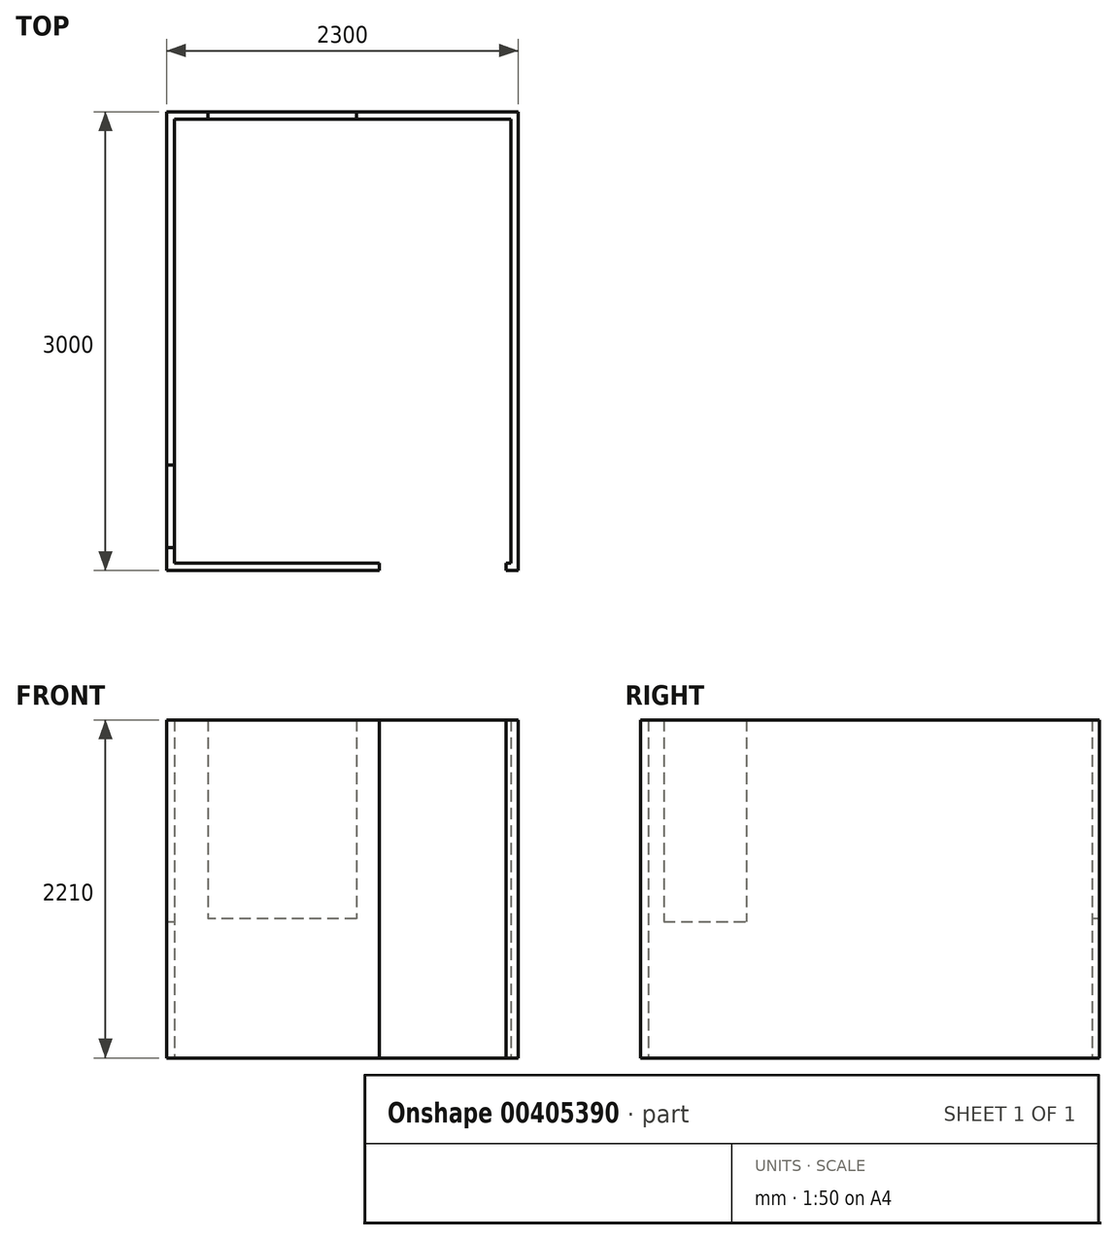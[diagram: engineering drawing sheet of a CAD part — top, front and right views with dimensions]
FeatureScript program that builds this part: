
annotation { "Feature Type Name" : "Feature", "Feature Type Description" : "" }
export const myFeature = defineFeature(function(context is Context, id is Id, definition is map)
    precondition{}
    {
        {
            var Q0;
            Q0=qCreatedBy(makeId("Top.planeOp"),FACE);
            var sketch = newSketch(context, id + "F0", { "sketchPlane" : qUnion([Q0])});
            skLineSegment(sketch, "E0.bottom", {"start": v(1100, -1450) * mm, "end": v(-1100, -1450) * mm});
            skLineSegment(sketch, "E0.top", {"start": v(1100, 1450) * mm, "end": v(-1100, 1450) * mm});
            skLineSegment(sketch, "E0.left", {"start": v(1100, -1450) * mm, "end": v(1100, 1450) * mm});
            skLineSegment(sketch, "E0.right", {"start": v(-1100, -1450) * mm, "end": v(-1100, 1450) * mm});
            skPoint(sketch, "E0.middle", {"position": v(0, 0) * mm});
            skLineSegment(sketch, "E1.0", {"start": v(-1150, -1500) * mm, "end": v(-1150, 1500) * mm});
            skLineSegment(sketch, "E1.1", {"start": v(1150, -1500) * mm, "end": v(-1150, -1500) * mm});
            skLineSegment(sketch, "E1.2", {"start": v(1150, -1500) * mm, "end": v(1150, 1500) * mm});
            skLineSegment(sketch, "E1.3", {"start": v(1150, 1500) * mm, "end": v(-1150, 1500) * mm});
            skLineSegment(sketch, "E2.bottom", {"start": v(1070, -1450) * mm, "end": v(240, -1450) * mm});
            skLineSegment(sketch, "E2.top", {"start": v(1070, -1500) * mm, "end": v(240, -1500) * mm});
            skLineSegment(sketch, "E2.left", {"start": v(1070, -1450) * mm, "end": v(1070, -1500) * mm});
            skLineSegment(sketch, "E2.right", {"start": v(240, -1450) * mm, "end": v(240, -1500) * mm});
            skSolve(sketch);
        }
        {
            var Q0;
            Q0=makeQuery(id+"F0.imprint","IMPRINT",FACE,{"disambiguationData":[TD([[makeQuery(id+"F0.imprint","IMPRINT",EDGE,{"derivedFrom":sQuery(id+"F0.wireOp",EDGE,"E0.top")}),-1.0]])]});
            extrude(context, id + "F1", {"entities" : qUnion([Q0]), "depth" : 890 * mm});
        }
        {
            var Q0;
            Q0=makeQuery(id+"F1.opExtrude","CAP_FACE",FACE,{"disambiguationData":[OSD([sQuery(id+"F0.wireOp",EDGE,"E0.bottom"),sQuery(id+"F0.wireOp",EDGE,"E0.top"),sQuery(id+"F0.wireOp",EDGE,"E0.left"),sQuery(id+"F0.wireOp",EDGE,"E0.right"),sQuery(id+"F0.wireOp",EDGE,"E1.0"),sQuery(id+"F0.wireOp",EDGE,"E1.1"),sQuery(id+"F0.wireOp",EDGE,"E1.2"),sQuery(id+"F0.wireOp",EDGE,"E1.3"),sQuery(id+"F0.wireOp",EDGE,"E2.left"),sQuery(id+"F0.wireOp",EDGE,"E2.right")])],"isStart":false});
            var sketch = newSketch(context, id + "F2", { "sketchPlane" : qUnion([Q0])});
            skLineSegment(sketch, "E3.bottom", {"start": v(-1150, -1350) * mm, "end": v(-1100, -1350) * mm});
            skLineSegment(sketch, "E3.top", {"start": v(-1150, -810) * mm, "end": v(-1100, -810) * mm});
            skLineSegment(sketch, "E3.left", {"start": v(-1150, -1350) * mm, "end": v(-1150, -810) * mm});
            skLineSegment(sketch, "E3.right", {"start": v(-1100, -1350) * mm, "end": v(-1100, -810) * mm});
            skSolve(sketch);
        }
        {
            var Q0;
            {var subQ8=sQuery(id+"F2.wireOp",EDGE,"E3.bottom");Q0=makeQuery(id+"F2.imprint","IMPRINT",FACE,{"disambiguationData":[TD([[makeQuery(id+"F2.imprint","IMPRINT",EDGE,{"derivedFrom":subQ8}),-1.0]])]});}
            var Q1;
            {var subQ5=sQuery(id+"F2.wireOp",EDGE,"E3.top");Q1=makeQuery(id+"F2.imprint","IMPRINT",FACE,{"disambiguationData":[TD([[makeQuery(id+"F2.imprint","IMPRINT",EDGE,{"derivedFrom":subQ5}),1.0]])]});}
            extrude(context, id + "F3", {"entities" : qUnion([Q0, Q1]), "operationType" : NewBodyOperationType.ADD, "depth" : 20 * mm});
        }
        {
            var Q0;
            Q0=makeQuery(id+"F3.opExtrude","CAP_FACE",FACE,{"disambiguationData":[OSD([sQuery(id+"F0.wireOp",EDGE,"E0.bottom"),sQuery(id+"F0.wireOp",EDGE,"E0.top"),sQuery(id+"F0.wireOp",EDGE,"E0.left"),sQuery(id+"F0.wireOp",EDGE,"E0.right"),sQuery(id+"F0.wireOp",EDGE,"E1.0"),sQuery(id+"F0.wireOp",EDGE,"E1.1"),sQuery(id+"F0.wireOp",EDGE,"E1.2"),sQuery(id+"F0.wireOp",EDGE,"E1.3"),sQuery(id+"F0.wireOp",EDGE,"E2.left"),sQuery(id+"F2.wireOp",EDGE,"E3.top")])],"isStart":false});
            var sketch = newSketch(context, id + "F4", { "sketchPlane" : qUnion([Q0])});
            skLineSegment(sketch, "E4.bottom", {"start": v(-880, 1500) * mm, "end": v(90, 1500) * mm});
            skLineSegment(sketch, "E4.top", {"start": v(-880, 1450) * mm, "end": v(90, 1450) * mm});
            skLineSegment(sketch, "E4.left", {"start": v(-880, 1500) * mm, "end": v(-880, 1450) * mm});
            skLineSegment(sketch, "E4.right", {"start": v(90, 1500) * mm, "end": v(90, 1450) * mm});
            skSolve(sketch);
        }
        {
            var Q0;
            Q0=makeQuery(id+"F3.opExtrude","CAP_FACE",FACE,{"disambiguationData":[OSD([sQuery(id+"F0.wireOp",EDGE,"E0.bottom"),sQuery(id+"F0.wireOp",EDGE,"E0.right"),sQuery(id+"F0.wireOp",EDGE,"E1.0"),sQuery(id+"F0.wireOp",EDGE,"E1.1"),sQuery(id+"F0.wireOp",EDGE,"E2.right"),sQuery(id+"F2.wireOp",EDGE,"E3.bottom")])],"isStart":false});
            var Q1;
            {var subQ9=sQuery(id+"F4.wireOp",EDGE,"E4.left");Q1=makeQuery(id+"F4.imprint","IMPRINT",FACE,{"disambiguationData":[TD([[makeQuery(id+"F4.imprint","IMPRINT",EDGE,{"derivedFrom":subQ9}),-1.0]])]});}
            var Q2;
            {var subQ6=sQuery(id+"F4.wireOp",EDGE,"E4.right");Q2=makeQuery(id+"F4.imprint","IMPRINT",FACE,{"disambiguationData":[TD([[makeQuery(id+"F4.imprint","IMPRINT",EDGE,{"derivedFrom":subQ6}),1.0]])]});}
            extrude(context, id + "F5", {"entities" : qUnion([Q0, Q1, Q2]), "operationType" : NewBodyOperationType.ADD, "depth" : 1300 * mm});
        }
    });
